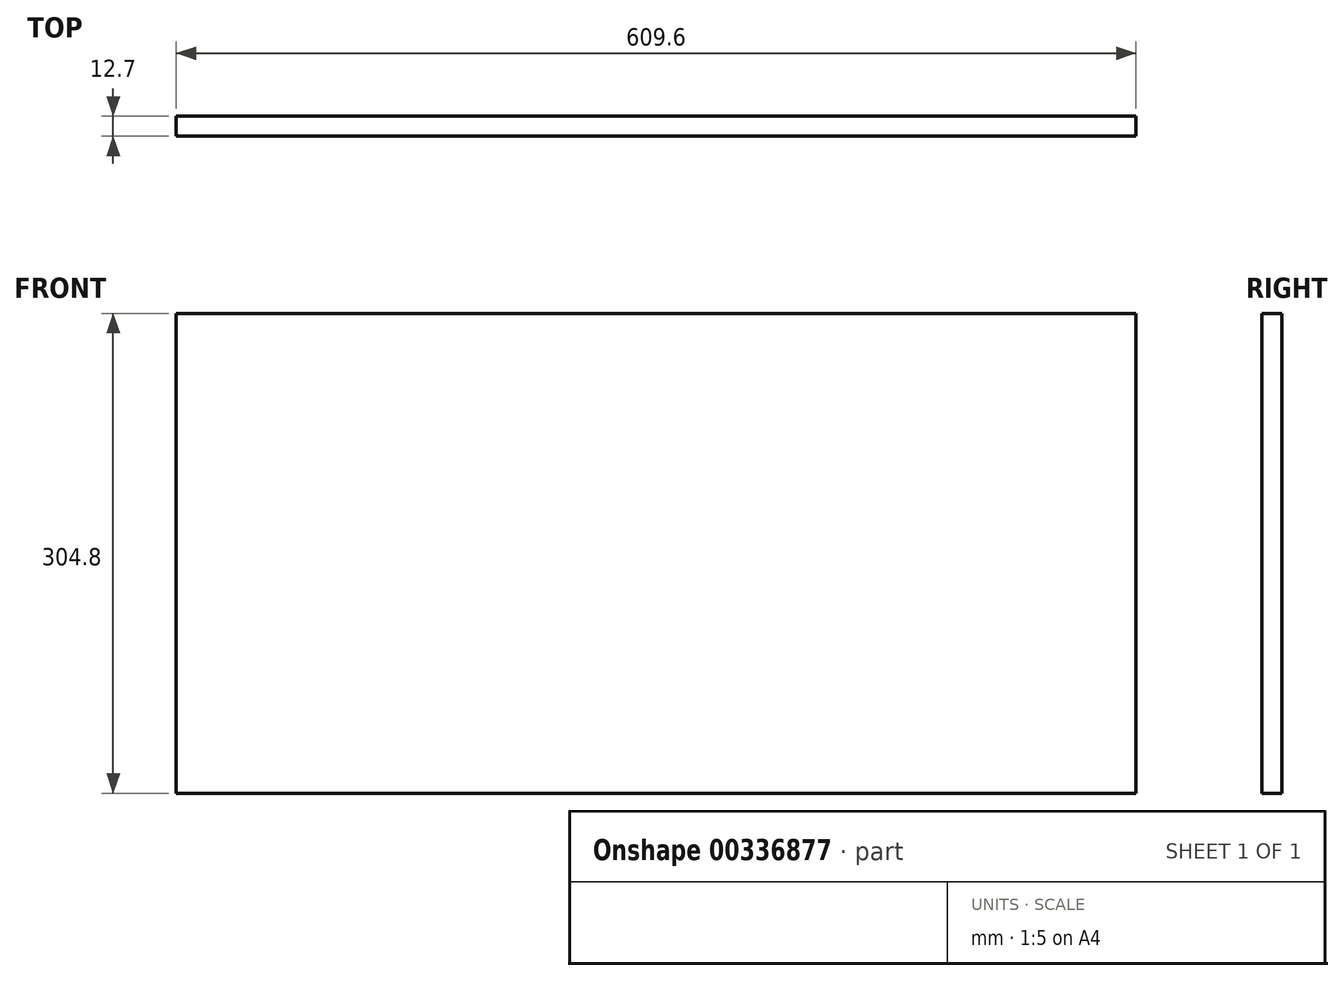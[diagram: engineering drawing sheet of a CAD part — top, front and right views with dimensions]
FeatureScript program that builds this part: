
annotation { "Feature Type Name" : "Feature", "Feature Type Description" : "" }
export const myFeature = defineFeature(function(context is Context, id is Id, definition is map)
    precondition{}
    {
        {
            var Q0;
            Q0=qCreatedBy(makeId("Front.planeOp"),FACE);
            var sketch = newSketch(context, id + "F0", { "sketchPlane" : qUnion([Q0])});
            skLineSegment(sketch, "E0.bottom", {"start": v(-168.63, 204.63) * mm, "end": v(440.97, 204.63) * mm});
            skLineSegment(sketch, "E0.top", {"start": v(-168.63, -100.17) * mm, "end": v(440.97, -100.17) * mm});
            skLineSegment(sketch, "E0.left", {"start": v(-168.63, 204.63) * mm, "end": v(-168.63, -100.17) * mm});
            skLineSegment(sketch, "E0.right", {"start": v(440.97, 204.63) * mm, "end": v(440.97, -100.17) * mm});
            skSolve(sketch);
        }
        {
            var Q0;
            Q0=makeQuery(id+"F0.imprint","IMPRINT",FACE,{"disambiguationData":[TD([[makeQuery(id+"F0.imprint","IMPRINT",EDGE,{"derivedFrom":sQuery(id+"F0.wireOp",EDGE,"E0.bottom")}),-1.0]])]});
            extrude(context, id + "F1", {"entities" : qUnion([Q0]), "depth" : 12.7 * mm});
        }
    });
